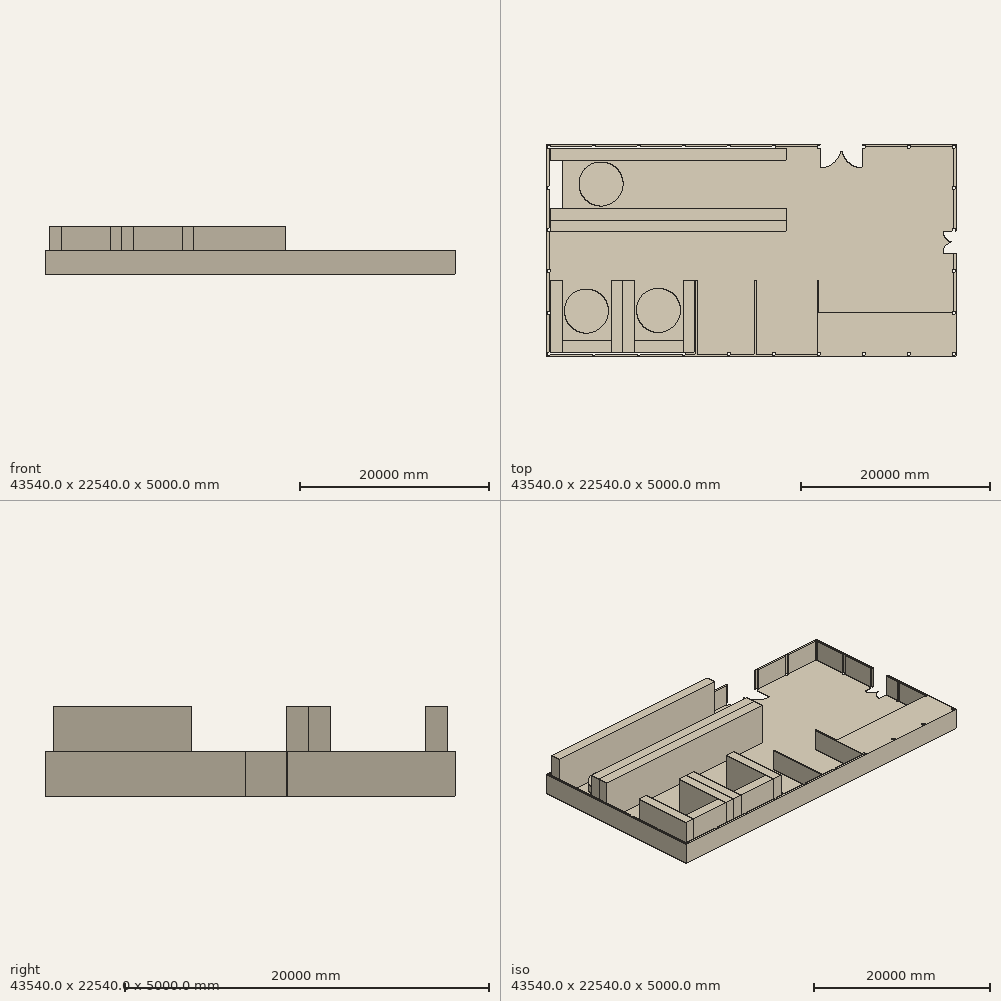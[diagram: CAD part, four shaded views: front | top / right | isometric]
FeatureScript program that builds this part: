
annotation { "Feature Type Name" : "Feature", "Feature Type Description" : "" }
export const myFeature = defineFeature(function(context is Context, id is Id, definition is map)
    precondition{}
    {
        {
            var Q0;
            Q0=qCreatedBy(makeId("Top.planeOp"),FACE);
            var sketch = newSketch(context, id + "F0", { "sketchPlane" : qUnion([Q0])});
            skLineSegment(sketch, "E0", {"start": v(0, 22000) * mm, "end": v(43000, 22000) * mm});
            skLineSegment(sketch, "E1", {"start": v(43000, 22000) * mm, "end": v(43000, 4400) * mm});
            skLineSegment(sketch, "E2", {"start": v(0, 22000) * mm, "end": v(0, 0) * mm});
            skLineSegment(sketch, "E3", {"start": v(0, 0) * mm, "end": v(28666.67, 0) * mm});
            skLineSegment(sketch, "E4.bottom", {"start": v(170, 22170) * mm, "end": v(-170, 22170) * mm});
            skLineSegment(sketch, "E4.top", {"start": v(170, 21830) * mm, "end": v(-170, 21830) * mm});
            skLineSegment(sketch, "E4.left", {"start": v(170, 22170) * mm, "end": v(170, 21830) * mm});
            skLineSegment(sketch, "E4.right", {"start": v(-170, 22170) * mm, "end": v(-170, 21830) * mm});
            skPoint(sketch, "E4.middle", {"position": v(0, 22000) * mm});
            skLineSegment(sketch, "E5.bottom", {"start": v(170, 170) * mm, "end": v(-170, 170) * mm});
            skLineSegment(sketch, "E5.top", {"start": v(170, -170) * mm, "end": v(-170, -170) * mm});
            skLineSegment(sketch, "E5.left", {"start": v(170, 170) * mm, "end": v(170, -170) * mm});
            skLineSegment(sketch, "E5.right", {"start": v(-170, 170) * mm, "end": v(-170, -170) * mm});
            skPoint(sketch, "E5.middle", {"position": v(0, 0) * mm});
            skLineSegment(sketch, "E6.0.1.0", {"start": v(170, 4230) * mm, "end": v(-170, 4230) * mm});
            skLineSegment(sketch, "E6.0.1.1", {"start": v(170, 4570) * mm, "end": v(-170, 4570) * mm});
            skLineSegment(sketch, "E6.0.1.2", {"start": v(170, 4570) * mm, "end": v(170, 4230) * mm});
            skLineSegment(sketch, "E6.0.1.3", {"start": v(-170, 4570) * mm, "end": v(-170, 4230) * mm});
            skLineSegment(sketch, "E6.0.2.0", {"start": v(170, 8630) * mm, "end": v(-170, 8630) * mm});
            skLineSegment(sketch, "E6.0.2.1", {"start": v(170, 8970) * mm, "end": v(-170, 8970) * mm});
            skLineSegment(sketch, "E6.0.2.2", {"start": v(170, 8970) * mm, "end": v(170, 8630) * mm});
            skLineSegment(sketch, "E6.0.2.3", {"start": v(-170, 8970) * mm, "end": v(-170, 8630) * mm});
            skLineSegment(sketch, "E6.0.3.0", {"start": v(170, 13030) * mm, "end": v(-170, 13030) * mm});
            skLineSegment(sketch, "E6.0.3.1", {"start": v(170, 13370) * mm, "end": v(-170, 13370) * mm});
            skLineSegment(sketch, "E6.0.3.2", {"start": v(170, 13370) * mm, "end": v(170, 13030) * mm});
            skLineSegment(sketch, "E6.0.3.3", {"start": v(-170, 13370) * mm, "end": v(-170, 13030) * mm});
            skLineSegment(sketch, "E6.0.4.0", {"start": v(170, 17430) * mm, "end": v(-170, 17430) * mm});
            skLineSegment(sketch, "E6.0.4.1", {"start": v(170, 17770) * mm, "end": v(-170, 17770) * mm});
            skLineSegment(sketch, "E6.0.4.2", {"start": v(170, 17770) * mm, "end": v(170, 17430) * mm});
            skLineSegment(sketch, "E6.0.4.3", {"start": v(-170, 17770) * mm, "end": v(-170, 17430) * mm});
            skLineSegment(sketch, "E7.0.1.0", {"start": v(43170, 4570) * mm, "end": v(43170, 4230) * mm});
            skPoint(sketch, "E7.0.1.1", {"position": v(43000, 4400) * mm});
            skLineSegment(sketch, "E7.0.1.2", {"start": v(42830, 4570) * mm, "end": v(42830, 4230) * mm});
            skLineSegment(sketch, "E7.0.1.4", {"start": v(43170, 4230) * mm, "end": v(42830, 4230) * mm});
            skLineSegment(sketch, "E7.0.1.5", {"start": v(43170, 4570) * mm, "end": v(42830, 4570) * mm});
            skLineSegment(sketch, "E7.0.2.0", {"start": v(43170, 8970) * mm, "end": v(43170, 8630) * mm});
            skPoint(sketch, "E7.0.2.1", {"position": v(43000, 8800) * mm});
            skLineSegment(sketch, "E7.0.2.2", {"start": v(42830, 8970) * mm, "end": v(42830, 8630) * mm});
            skLineSegment(sketch, "E7.0.2.4", {"start": v(43170, 8630) * mm, "end": v(42830, 8630) * mm});
            skLineSegment(sketch, "E7.0.2.5", {"start": v(43170, 8970) * mm, "end": v(42830, 8970) * mm});
            skLineSegment(sketch, "E7.0.3.0", {"start": v(43170, 13370) * mm, "end": v(43170, 13030) * mm});
            skPoint(sketch, "E7.0.3.1", {"position": v(43000, 13200) * mm});
            skLineSegment(sketch, "E7.0.3.2", {"start": v(42830, 13370) * mm, "end": v(42830, 13030) * mm});
            skLineSegment(sketch, "E7.0.3.4", {"start": v(43170, 13030) * mm, "end": v(42830, 13030) * mm});
            skLineSegment(sketch, "E7.0.3.5", {"start": v(43170, 13370) * mm, "end": v(42830, 13370) * mm});
            skLineSegment(sketch, "E7.0.4.0", {"start": v(43170, 17770) * mm, "end": v(43170, 17430) * mm});
            skPoint(sketch, "E7.0.4.1", {"position": v(43000, 17600) * mm});
            skLineSegment(sketch, "E7.0.4.2", {"start": v(42830, 17770) * mm, "end": v(42830, 17430) * mm});
            skLineSegment(sketch, "E7.0.4.4", {"start": v(43170, 17430) * mm, "end": v(42830, 17430) * mm});
            skLineSegment(sketch, "E7.0.4.5", {"start": v(43170, 17770) * mm, "end": v(42830, 17770) * mm});
            skPoint(sketch, "E8.1.0.0", {"position": v(4777.78, 22000) * mm});
            skLineSegment(sketch, "E8.1.0.1", {"start": v(4947.78, 22170) * mm, "end": v(4607.78, 22170) * mm});
            skLineSegment(sketch, "E8.1.0.2", {"start": v(4947.78, 22170) * mm, "end": v(4947.78, 21830) * mm});
            skLineSegment(sketch, "E8.1.0.3", {"start": v(4607.78, 22170) * mm, "end": v(4607.78, 21830) * mm});
            skLineSegment(sketch, "E8.1.0.4", {"start": v(4947.78, 21830) * mm, "end": v(4607.78, 21830) * mm});
            skPoint(sketch, "E8.2.0.0", {"position": v(9555.56, 22000) * mm});
            skLineSegment(sketch, "E8.2.0.1", {"start": v(9725.56, 22170) * mm, "end": v(9385.56, 22170) * mm});
            skLineSegment(sketch, "E8.2.0.2", {"start": v(9725.56, 22170) * mm, "end": v(9725.56, 21830) * mm});
            skLineSegment(sketch, "E8.2.0.3", {"start": v(9385.56, 22170) * mm, "end": v(9385.56, 21830) * mm});
            skLineSegment(sketch, "E8.2.0.4", {"start": v(9725.56, 21830) * mm, "end": v(9385.56, 21830) * mm});
            skPoint(sketch, "E8.3.0.0", {"position": v(14333.33, 22000) * mm});
            skLineSegment(sketch, "E8.3.0.1", {"start": v(14503.33, 22170) * mm, "end": v(14163.33, 22170) * mm});
            skLineSegment(sketch, "E8.3.0.2", {"start": v(14503.33, 22170) * mm, "end": v(14503.33, 21830) * mm});
            skLineSegment(sketch, "E8.3.0.3", {"start": v(14163.33, 22170) * mm, "end": v(14163.33, 21830) * mm});
            skLineSegment(sketch, "E8.3.0.4", {"start": v(14503.33, 21830) * mm, "end": v(14163.33, 21830) * mm});
            skPoint(sketch, "E8.4.0.0", {"position": v(19111.11, 22000) * mm});
            skLineSegment(sketch, "E8.4.0.1", {"start": v(19281.11, 22170) * mm, "end": v(18941.11, 22170) * mm});
            skLineSegment(sketch, "E8.4.0.2", {"start": v(19281.11, 22170) * mm, "end": v(19281.11, 21830) * mm});
            skLineSegment(sketch, "E8.4.0.3", {"start": v(18941.11, 22170) * mm, "end": v(18941.11, 21830) * mm});
            skLineSegment(sketch, "E8.4.0.4", {"start": v(19281.11, 21830) * mm, "end": v(18941.11, 21830) * mm});
            skPoint(sketch, "E8.5.0.0", {"position": v(23888.89, 22000) * mm});
            skLineSegment(sketch, "E8.5.0.1", {"start": v(24058.89, 22170) * mm, "end": v(23718.89, 22170) * mm});
            skLineSegment(sketch, "E8.5.0.2", {"start": v(24058.89, 22170) * mm, "end": v(24058.89, 21830) * mm});
            skLineSegment(sketch, "E8.5.0.3", {"start": v(23718.89, 22170) * mm, "end": v(23718.89, 21830) * mm});
            skLineSegment(sketch, "E8.5.0.4", {"start": v(24058.89, 21830) * mm, "end": v(23718.89, 21830) * mm});
            skPoint(sketch, "E8.6.0.0", {"position": v(28666.67, 22000) * mm});
            skLineSegment(sketch, "E8.6.0.1", {"start": v(28836.67, 22170) * mm, "end": v(28496.67, 22170) * mm});
            skLineSegment(sketch, "E8.6.0.2", {"start": v(28836.67, 22170) * mm, "end": v(28836.67, 21830) * mm});
            skLineSegment(sketch, "E8.6.0.3", {"start": v(28496.67, 22170) * mm, "end": v(28496.67, 21830) * mm});
            skLineSegment(sketch, "E8.6.0.4", {"start": v(28836.67, 21830) * mm, "end": v(28496.67, 21830) * mm});
            skPoint(sketch, "E8.7.0.0", {"position": v(33444.44, 22000) * mm});
            skLineSegment(sketch, "E8.7.0.1", {"start": v(33614.44, 22170) * mm, "end": v(33274.44, 22170) * mm});
            skLineSegment(sketch, "E8.7.0.2", {"start": v(33614.44, 22170) * mm, "end": v(33614.44, 21830) * mm});
            skLineSegment(sketch, "E8.7.0.3", {"start": v(33274.44, 22170) * mm, "end": v(33274.44, 21830) * mm});
            skLineSegment(sketch, "E8.7.0.4", {"start": v(33614.44, 21830) * mm, "end": v(33274.44, 21830) * mm});
            skPoint(sketch, "E8.8.0.0", {"position": v(38222.22, 22000) * mm});
            skLineSegment(sketch, "E8.8.0.1", {"start": v(38392.22, 22170) * mm, "end": v(38052.22, 22170) * mm});
            skLineSegment(sketch, "E8.8.0.2", {"start": v(38392.22, 22170) * mm, "end": v(38392.22, 21830) * mm});
            skLineSegment(sketch, "E8.8.0.3", {"start": v(38052.22, 22170) * mm, "end": v(38052.22, 21830) * mm});
            skLineSegment(sketch, "E8.8.0.4", {"start": v(38392.22, 21830) * mm, "end": v(38052.22, 21830) * mm});
            skPoint(sketch, "E8.9.0.0", {"position": v(43000, 22000) * mm});
            skLineSegment(sketch, "E8.9.0.1", {"start": v(43170, 22170) * mm, "end": v(42830, 22170) * mm});
            skLineSegment(sketch, "E8.9.0.2", {"start": v(43170, 22170) * mm, "end": v(43170, 21830) * mm});
            skLineSegment(sketch, "E8.9.0.3", {"start": v(42830, 22170) * mm, "end": v(42830, 21830) * mm});
            skLineSegment(sketch, "E8.9.0.4", {"start": v(43170, 21830) * mm, "end": v(42830, 21830) * mm});
            skLineSegment(sketch, "E9.1.0.0", {"start": v(4947.78, 170) * mm, "end": v(4607.78, 170) * mm});
            skLineSegment(sketch, "E9.1.0.1", {"start": v(4947.78, -170) * mm, "end": v(4607.78, -170) * mm});
            skPoint(sketch, "E9.1.0.2", {"position": v(4777.78, 0) * mm});
            skLineSegment(sketch, "E9.1.0.3", {"start": v(4607.78, 170) * mm, "end": v(4607.78, -170) * mm});
            skLineSegment(sketch, "E9.1.0.4", {"start": v(4947.78, 170) * mm, "end": v(4947.78, -170) * mm});
            skLineSegment(sketch, "E9.2.0.0", {"start": v(9725.56, 170) * mm, "end": v(9385.56, 170) * mm});
            skLineSegment(sketch, "E9.2.0.1", {"start": v(9725.56, -170) * mm, "end": v(9385.56, -170) * mm});
            skPoint(sketch, "E9.2.0.2", {"position": v(9555.56, 0) * mm});
            skLineSegment(sketch, "E9.2.0.3", {"start": v(9385.56, 170) * mm, "end": v(9385.56, -170) * mm});
            skLineSegment(sketch, "E9.2.0.4", {"start": v(9725.56, 170) * mm, "end": v(9725.56, -170) * mm});
            skLineSegment(sketch, "E9.3.0.0", {"start": v(14503.33, 170) * mm, "end": v(14163.33, 170) * mm});
            skLineSegment(sketch, "E9.3.0.1", {"start": v(14503.33, -170) * mm, "end": v(14163.33, -170) * mm});
            skPoint(sketch, "E9.3.0.2", {"position": v(14333.33, 0) * mm});
            skLineSegment(sketch, "E9.3.0.3", {"start": v(14163.33, 170) * mm, "end": v(14163.33, -170) * mm});
            skLineSegment(sketch, "E9.3.0.4", {"start": v(14503.33, 170) * mm, "end": v(14503.33, -170) * mm});
            skLineSegment(sketch, "E9.4.0.0", {"start": v(19281.11, 170) * mm, "end": v(18941.11, 170) * mm});
            skLineSegment(sketch, "E9.4.0.1", {"start": v(19281.11, -170) * mm, "end": v(18941.11, -170) * mm});
            skPoint(sketch, "E9.4.0.2", {"position": v(19111.11, 0) * mm});
            skLineSegment(sketch, "E9.4.0.3", {"start": v(18941.11, 170) * mm, "end": v(18941.11, -170) * mm});
            skLineSegment(sketch, "E9.4.0.4", {"start": v(19281.11, 170) * mm, "end": v(19281.11, -170) * mm});
            skLineSegment(sketch, "E9.5.0.0", {"start": v(24058.89, 170) * mm, "end": v(23718.89, 170) * mm});
            skLineSegment(sketch, "E9.5.0.1", {"start": v(24058.89, -170) * mm, "end": v(23718.89, -170) * mm});
            skPoint(sketch, "E9.5.0.2", {"position": v(23888.89, 0) * mm});
            skLineSegment(sketch, "E9.5.0.3", {"start": v(23718.89, 170) * mm, "end": v(23718.89, -170) * mm});
            skLineSegment(sketch, "E9.5.0.4", {"start": v(24058.89, 170) * mm, "end": v(24058.89, -170) * mm});
            skLineSegment(sketch, "E9.6.0.0", {"start": v(28836.67, 170) * mm, "end": v(28496.67, 170) * mm});
            skLineSegment(sketch, "E9.6.0.1", {"start": v(28836.67, -170) * mm, "end": v(28496.67, -170) * mm});
            skPoint(sketch, "E9.6.0.2", {"position": v(28666.67, 0) * mm});
            skLineSegment(sketch, "E9.6.0.3", {"start": v(28496.67, 170) * mm, "end": v(28496.67, -170) * mm});
            skLineSegment(sketch, "E9.6.0.4", {"start": v(28836.67, 170) * mm, "end": v(28836.67, -170) * mm});
            skLineSegment(sketch, "E9.7.0.0", {"start": v(33614.44, 170) * mm, "end": v(33274.44, 170) * mm});
            skLineSegment(sketch, "E9.7.0.1", {"start": v(33614.44, -170) * mm, "end": v(33274.44, -170) * mm});
            skPoint(sketch, "E9.7.0.2", {"position": v(33444.44, 0) * mm});
            skLineSegment(sketch, "E9.7.0.3", {"start": v(33274.44, 170) * mm, "end": v(33274.44, -170) * mm});
            skLineSegment(sketch, "E9.7.0.4", {"start": v(33614.44, 170) * mm, "end": v(33614.44, -170) * mm});
            skLineSegment(sketch, "E9.8.0.0", {"start": v(38392.22, 170) * mm, "end": v(38052.22, 170) * mm});
            skLineSegment(sketch, "E9.8.0.1", {"start": v(38392.22, -170) * mm, "end": v(38052.22, -170) * mm});
            skPoint(sketch, "E9.8.0.2", {"position": v(38222.22, 0) * mm});
            skLineSegment(sketch, "E9.8.0.3", {"start": v(38052.22, 170) * mm, "end": v(38052.22, -170) * mm});
            skLineSegment(sketch, "E9.8.0.4", {"start": v(38392.22, 170) * mm, "end": v(38392.22, -170) * mm});
            skLineSegment(sketch, "E9.9.0.0", {"start": v(43170, 170) * mm, "end": v(42830, 170) * mm});
            skLineSegment(sketch, "E9.9.0.1", {"start": v(43170, -170) * mm, "end": v(42830, -170) * mm});
            skPoint(sketch, "E9.9.0.2", {"position": v(43000, 0) * mm});
            skLineSegment(sketch, "E9.9.0.3", {"start": v(42830, 170) * mm, "end": v(42830, -170) * mm});
            skLineSegment(sketch, "E9.9.0.4", {"start": v(43170, 170) * mm, "end": v(43170, -170) * mm});
            skLineSegment(sketch, "E10.bottom", {"start": v(28836.67, 22000) * mm, "end": v(33274.44, 22000) * mm});
            skLineSegment(sketch, "E10.left", {"start": v(28836.67, 22000) * mm, "end": v(28836.67, 19781.11) * mm});
            skLineSegment(sketch, "E10.right", {"start": v(33274.44, 22000) * mm, "end": v(33274.44, 19781.11) * mm});
            skLineSegment(sketch, "E11", {"start": v(28666.67, 0) * mm, "end": v(43000, 0) * mm});
            skLineSegment(sketch, "E12", {"start": v(43000, 4400) * mm, "end": v(43000, 0) * mm});
            skLineSegment(sketch, "E13", {"start": v(43000, 4400) * mm, "end": v(28666.67, 4400) * mm});
            skLineSegment(sketch, "E14", {"start": v(28666.67, 4400) * mm, "end": v(28666.67, 0) * mm});
            skLineSegment(sketch, "E15", {"start": v(33444.44, 0) * mm, "end": v(33444.44, 4400) * mm});
            skLineSegment(sketch, "E16.top", {"start": v(43000, 10730) * mm, "end": v(41850, 10730) * mm});
            skLineSegment(sketch, "E16.left", {"start": v(43000, 13030) * mm, "end": v(43000, 10730) * mm});
            skLineSegment(sketch, "E17.top", {"start": v(69479.6, 14575.56) * mm, "end": v(70779.6, 14575.56) * mm});
            skLineSegment(sketch, "E17.left", {"start": v(69479.6, 17475.56) * mm, "end": v(69479.6, 14575.56) * mm});
            skLineSegment(sketch, "E17.right", {"start": v(70779.6, 17475.56) * mm, "end": v(70779.6, 14575.56) * mm});
            skLineSegment(sketch, "E18", {"start": v(69479.6, 17475.56) * mm, "end": v(69704.6, 17475.56) * mm});
            skLineSegment(sketch, "E19.MirrorCS", {"start": v(69904.6, 17475.56) * mm, "end": v(69904.6, 19075.56) * mm});
            skLineSegment(sketch, "E20", {"start": v(69704.6, 19075.56) * mm, "end": v(69704.6, 17475.56) * mm});
            skLineSegment(sketch, "E21.MirrorCS", {"start": v(70354.6, 17475.56) * mm, "end": v(70354.6, 19075.56) * mm});
            skLineSegment(sketch, "E22.MirrorCS", {"start": v(70554.6, 19075.56) * mm, "end": v(70554.6, 17475.56) * mm});
            skLineSegment(sketch, "E23", {"start": v(69704.6, 19075.56) * mm, "end": v(69904.6, 19075.56) * mm});
            skLineSegment(sketch, "E24.trimOffspring", {"start": v(70354.6, 19075.56) * mm, "end": v(70554.6, 19075.56) * mm});
            skLineSegment(sketch, "E25.bottom", {"start": v(64498.07, 14575.56) * mm, "end": v(65798.07, 14575.56) * mm});
            skLineSegment(sketch, "E25.top", {"start": v(64498.07, 19075.56) * mm, "end": v(65798.07, 19075.56) * mm});
            skLineSegment(sketch, "E25.left", {"start": v(64498.07, 14575.56) * mm, "end": v(64498.07, 19075.56) * mm});
            skLineSegment(sketch, "E25.right", {"start": v(65798.07, 14575.56) * mm, "end": v(65798.07, 19075.56) * mm});
            skLineSegment(sketch, "E26.trimOffspring", {"start": v(69904.6, 17475.56) * mm, "end": v(70354.6, 17475.56) * mm});
            skLineSegment(sketch, "E27.trimOffspring", {"start": v(70554.6, 17475.56) * mm, "end": v(70779.6, 17475.56) * mm});
            skLineSegment(sketch, "E28", {"start": v(30055.67, 19781.11) * mm, "end": v(30055.67, 11370) * mm});
            skLineSegment(sketch, "E29", {"start": v(30055.67, 11370) * mm, "end": v(0, 11370) * mm});
            skLineSegment(sketch, "E30", {"start": v(0, 9370) * mm, "end": v(32055.67, 9370) * mm});
            skLineSegment(sketch, "E31", {"start": v(32055.67, 9370) * mm, "end": v(32055.67, 19781.11) * mm});
            skLineSegment(sketch, "E32", {"start": v(31055.56, 19781.11) * mm, "end": v(31055.56, 10370) * mm, "construction": true});
            skLineSegment(sketch, "E33", {"start": v(31055.56, 10370) * mm, "end": v(0, 10370) * mm, "construction": true});
            skArc(sketch, "E34", {"start": v(43000, 11880) * mm, "mid": v(42186.83, 12216.83) * mm, "end": v(41850, 13030) * mm});
            skLineSegment(sketch, "E35", {"start": v(41850, 13030) * mm, "end": v(43000, 13030) * mm});
            skArc(sketch, "E36", {"start": v(43000, 11880) * mm, "mid": v(42186.83, 11543.17) * mm, "end": v(41850, 10730) * mm});
            skArc(sketch, "E37", {"start": v(31055.56, 22000) * mm, "mid": v(30405.66, 20431) * mm, "end": v(28836.67, 19781.11) * mm});
            skArc(sketch, "E38", {"start": v(31055.56, 22000) * mm, "mid": v(31705.45, 20431) * mm, "end": v(33274.44, 19781.11) * mm});
            skLineSegment(sketch, "E39", {"start": v(28836.67, 19781.11) * mm, "end": v(33274.44, 19781.11) * mm, "construction": true});
            skPoint(sketch, "E40", {"position": v(32055.67, 14575.56) * mm});
            skLineSegment(sketch, "E41", {"start": v(28666.67, 4400) * mm, "end": v(28666.67, 7770) * mm});
            skLineSegment(sketch, "E42.3", {"start": v(15589.43, -270) * mm, "end": v(15589.43, 7770) * mm});
            skLineSegment(sketch, "E43.0", {"start": v(22016.67, 7770) * mm, "end": v(22016.67, -270) * mm});
            skLineSegment(sketch, "E44.bottom", {"start": v(-270, 22270) * mm, "end": v(43270, 22270) * mm});
            skLineSegment(sketch, "E44.top", {"start": v(-270, -270) * mm, "end": v(43270, -270) * mm});
            skLineSegment(sketch, "E44.left", {"start": v(-270, 22270) * mm, "end": v(-270, -270) * mm});
            skLineSegment(sketch, "E44.right", {"start": v(43270, 22270) * mm, "end": v(43270, -270) * mm});
            skLineSegment(sketch, "E45", {"start": v(33274.44, 22170) * mm, "end": v(33274.44, 22270) * mm});
            skLineSegment(sketch, "E46", {"start": v(28836.67, 22170) * mm, "end": v(28836.67, 22270) * mm});
            skLineSegment(sketch, "E47", {"start": v(43170, 13030) * mm, "end": v(43270, 13030) * mm});
            skLineSegment(sketch, "E48", {"start": v(43000, 10730) * mm, "end": v(43270, 10730) * mm});
            skLineSegment(sketch, "E49.bottom", {"start": v(170, 21830) * mm, "end": v(25170, 21830) * mm});
            skLineSegment(sketch, "E49.top", {"start": v(170, 20610) * mm, "end": v(25170, 20610) * mm});
            skLineSegment(sketch, "E49.left", {"start": v(170, 21830) * mm, "end": v(170, 20610) * mm});
            skLineSegment(sketch, "E49.right", {"start": v(25170, 21830) * mm, "end": v(25170, 20610) * mm});
            skLineSegment(sketch, "E50.bottom", {"start": v(170, 15410) * mm, "end": v(25170, 15410) * mm});
            skLineSegment(sketch, "E50.top", {"start": v(170, 14190) * mm, "end": v(25170, 14190) * mm});
            skLineSegment(sketch, "E50.left", {"start": v(170, 15410) * mm, "end": v(170, 14190) * mm});
            skLineSegment(sketch, "E50.right", {"start": v(25170, 15410) * mm, "end": v(25170, 14190) * mm});
            skLineSegment(sketch, "E51", {"start": v(170, 14190) * mm, "end": v(170, 12970) * mm});
            skLineSegment(sketch, "E52", {"start": v(170, 12970) * mm, "end": v(25170, 12970) * mm});
            skLineSegment(sketch, "E53", {"start": v(25170, 12970) * mm, "end": v(25170, 14190) * mm});
            skLineSegment(sketch, "E54.bottom", {"start": v(170, 170) * mm, "end": v(1390, 170) * mm});
            skLineSegment(sketch, "E54.top", {"start": v(170, 7770) * mm, "end": v(1390, 7770) * mm});
            skLineSegment(sketch, "E54.left", {"start": v(170, 170) * mm, "end": v(170, 7770) * mm});
            skLineSegment(sketch, "E54.right", {"start": v(1390, 170) * mm, "end": v(1390, 7770) * mm});
            skLineSegment(sketch, "E55.bottom", {"start": v(1390, 170) * mm, "end": v(6590, 170) * mm});
            skLineSegment(sketch, "E55.top", {"start": v(1390, 1390) * mm, "end": v(6590, 1390) * mm});
            skLineSegment(sketch, "E55.left", {"start": v(1390, 170) * mm, "end": v(1390, 1390) * mm});
            skLineSegment(sketch, "E55.right", {"start": v(6590, 170) * mm, "end": v(6590, 1390) * mm});
            skLineSegment(sketch, "E56.bottom", {"start": v(6590, 170) * mm, "end": v(7810, 170) * mm});
            skLineSegment(sketch, "E56.top", {"start": v(6590, 7770) * mm, "end": v(7810, 7770) * mm});
            skLineSegment(sketch, "E56.left", {"start": v(6590, 170) * mm, "end": v(6590, 7770) * mm});
            skLineSegment(sketch, "E56.right", {"start": v(7810, 170) * mm, "end": v(7810, 7770) * mm});
            skLineSegment(sketch, "E57.bottom", {"start": v(7810, 170) * mm, "end": v(9030, 170) * mm});
            skLineSegment(sketch, "E57.top", {"start": v(7810, 7770) * mm, "end": v(9030, 7770) * mm});
            skLineSegment(sketch, "E57.right", {"start": v(9030, 170) * mm, "end": v(9030, 7770) * mm});
            skLineSegment(sketch, "E58.bottom", {"start": v(9030, 170) * mm, "end": v(14230, 170) * mm});
            skLineSegment(sketch, "E58.top", {"start": v(9030, 1390) * mm, "end": v(14230, 1390) * mm});
            skLineSegment(sketch, "E58.left", {"start": v(9030, 170) * mm, "end": v(9030, 1390) * mm});
            skLineSegment(sketch, "E58.right", {"start": v(14230, 170) * mm, "end": v(14230, 1390) * mm});
            skLineSegment(sketch, "E59.bottom", {"start": v(14230, 170) * mm, "end": v(15450, 170) * mm});
            skLineSegment(sketch, "E59.top", {"start": v(14230, 7770) * mm, "end": v(15450, 7770) * mm});
            skLineSegment(sketch, "E59.left", {"start": v(14230, 170) * mm, "end": v(14230, 7770) * mm});
            skLineSegment(sketch, "E59.right", {"start": v(15450, 170) * mm, "end": v(15450, 7770) * mm});
            skLineSegment(sketch, "E60.bottom", {"start": v(170, 20610) * mm, "end": v(1390, 20610) * mm});
            skLineSegment(sketch, "E60.top", {"start": v(170, 15410) * mm, "end": v(1390, 15410) * mm});
            skLineSegment(sketch, "E60.left", {"start": v(170, 20610) * mm, "end": v(170, 15410) * mm});
            skLineSegment(sketch, "E60.right", {"start": v(1390, 20610) * mm, "end": v(1390, 15410) * mm});
            skLineSegment(sketch, "E61", {"start": v(64498.07, 19075.56) * mm, "end": v(65798.07, 14575.56) * mm, "construction": true});
            skCircle(sketch, "E62", {"center": v(5527.86, 18056.06) * mm, "radius": 2342 * mm});
            skPoint(sketch, "E42.0.start.orphan", {"position": v(28516.67, -13106.31) * mm});
            skLineSegment(sketch, "E63", {"start": v(15589.43, 7770) * mm, "end": v(22016.67, 7770) * mm});
            skLineSegment(sketch, "E64", {"start": v(22016.67, 7770) * mm, "end": v(28666.67, 7770) * mm});
            skLineSegment(sketch, "E65", {"start": v(15739.43, -270) * mm, "end": v(15739.43, 7770) * mm});
            skLineSegment(sketch, "E66", {"start": v(15589.43, 7620) * mm, "end": v(28666.67, 7620) * mm});
            skLineSegment(sketch, "E67", {"start": v(28516.67, 7770) * mm, "end": v(28516.67, -270) * mm});
            skLineSegment(sketch, "E68", {"start": v(21866.67, 7770) * mm, "end": v(21866.67, -270) * mm});
            skCircle(sketch, "E69", {"center": v(11629.68, 4634.86) * mm, "radius": 2342 * mm});
            skCircle(sketch, "E70", {"center": v(3977.19, 4560.05) * mm, "radius": 2342 * mm});
            skSolve(sketch);
        }
        {
            var Q0;
            {var subQ69=sQuery(id+"F0.wireOp",EDGE,"E6.0.2.2");Q0=makeQuery(id+"F0.imprint","IMPRINT",FACE,{"disambiguationData":[TD([[makeQuery(id+"F0.imprint","IMPRINT",EDGE,{"derivedFrom":subQ69}),1.0]])]});}
            var Q1;
            {var subQ0=sQuery(id+"F0.wireOp",EDGE,"E9.4.0.0");Q1=makeQuery(id+"F0.imprint","IMPRINT",FACE,{"disambiguationData":[TD([[makeQuery(id+"F0.imprint","IMPRINT",EDGE,{"derivedFrom":subQ0}),-1.0]])]});}
            var Q2;
            {var subQ1=sQuery(id+"F0.wireOp",EDGE,"E9.5.0.0");Q2=makeQuery(id+"F0.imprint","IMPRINT",FACE,{"disambiguationData":[TD([[makeQuery(id+"F0.imprint","IMPRINT",EDGE,{"derivedFrom":subQ1}),-1.0]])]});}
            var Q3;
            {var subQ1=sQuery(id+"F0.wireOp",EDGE,"E43.0");var subQ3=sQuery(id+"F0.wireOp",EDGE,"E66");var subQ4=makeQuery(id+"F0.imprint","INTERSECT",VERTEX,{"derivedFrom":[subQ1,subQ3]});Q3=makeQuery(id+"F0.imprint","IMPRINT",FACE,{"disambiguationData":[TD([[makeQuery(id+"F0.imprint","IMPRINT",EDGE,{"disambiguationData":[TD([[subQ4,-1.0]])],"derivedFrom":subQ3}),1.0]])]});}
            var Q4;
            {var subQ0=sQuery(id+"F0.wireOp",EDGE,"E65");var subQ1=sQuery(id+"F0.wireOp",EDGE,"E63");var subQ2=makeQuery(id+"F0.imprint","INTERSECT",VERTEX,{"derivedFrom":[subQ1,subQ0]});Q4=makeQuery(id+"F0.imprint","IMPRINT",FACE,{"disambiguationData":[TD([[makeQuery(id+"F0.imprint","IMPRINT",EDGE,{"disambiguationData":[TD([[subQ2,-1.0]])],"derivedFrom":subQ1}),-1.0]])]});}
            extrude(context, id + "F1", {"entities" : qUnion([Q0, Q1, Q2, Q3, Q4]), "depth" : 25 * mm, "offsetDistance" : 25 * mm});
        }
        {
            var Q0;
            Q0=makeQuery(id+"F0.imprint","IMPRINT",FACE,{"disambiguationData":[TD([[makeQuery(id+"F0.imprint","IMPRINT",EDGE,{"derivedFrom":sQuery(id+"F0.wireOp",EDGE,"E50.bottom")}),-1.0]])]});
            var Q1;
            {var subQ3=sQuery(id+"F0.wireOp",EDGE,"E54.bottom");Q1=makeQuery(id+"F0.imprint","IMPRINT",FACE,{"disambiguationData":[TD([[makeQuery(id+"F0.imprint","IMPRINT",EDGE,{"derivedFrom":subQ3}),1.0]])]});}
            var Q2;
            {var subQ3=sQuery(id+"F0.wireOp",EDGE,"E56.bottom");Q2=makeQuery(id+"F0.imprint","IMPRINT",FACE,{"disambiguationData":[TD([[makeQuery(id+"F0.imprint","IMPRINT",EDGE,{"derivedFrom":subQ3}),1.0]])]});}
            var Q3;
            Q3=makeQuery(id+"F0.imprint","IMPRINT",FACE,{"disambiguationData":[TD([[makeQuery(id+"F0.imprint","IMPRINT",EDGE,{"derivedFrom":sQuery(id+"F0.wireOp",EDGE,"E49.top")}),1.0]])]});
            var Q4;
            {var subQ4=sQuery(id+"F0.wireOp",EDGE,"E59.top");Q4=makeQuery(id+"F0.imprint","IMPRINT",FACE,{"disambiguationData":[TD([[makeQuery(id+"F0.imprint","IMPRINT",EDGE,{"derivedFrom":subQ4}),-1.0]])]});}
            extrude(context, id + "F2", {"entities" : qUnion([Q0, Q1, Q2, Q3, Q4]), "depth" : 5000 * mm, "offsetDistance" : 25 * mm});
        }
        {
            var Q0;
            {var subQ0=sQuery(id+"F0.wireOp",EDGE,"E55.top");Q0=makeQuery(id+"F0.imprint","IMPRINT",FACE,{"disambiguationData":[TD([[makeQuery(id+"F0.imprint","IMPRINT",EDGE,{"derivedFrom":subQ0}),-1.0]])]});}
            var Q1;
            Q1=makeQuery(id+"F0.imprint","IMPRINT",FACE,{"disambiguationData":[TD([[makeQuery(id+"F0.imprint","IMPRINT",EDGE,{"derivedFrom":sQuery(id+"F0.wireOp",EDGE,"E57.bottom")}),1.0]])]});
            var Q2;
            {var subQ3=sQuery(id+"F0.wireOp",EDGE,"E50.top");Q2=makeQuery(id+"F0.imprint","IMPRINT",FACE,{"disambiguationData":[TD([[makeQuery(id+"F0.imprint","IMPRINT",EDGE,{"derivedFrom":subQ3}),-1.0]])]});}
            var Q3;
            {var subQ3=sQuery(id+"F0.wireOp",EDGE,"E60.bottom");Q3=makeQuery(id+"F0.imprint","IMPRINT",FACE,{"disambiguationData":[TD([[makeQuery(id+"F0.imprint","IMPRINT",EDGE,{"derivedFrom":subQ3}),-1.0]])]});}
            extrude(context, id + "F3", {"entities" : qUnion([Q0, Q1, Q2, Q3]), "depth" : 5000 * mm, "offsetDistance" : 25 * mm});
        }
        {
            var Q0;
            {var subQ7=sQuery(id+"F0.wireOp",EDGE,"E58.top");Q0=makeQuery(id+"F0.imprint","IMPRINT",FACE,{"disambiguationData":[TD([[makeQuery(id+"F0.imprint","IMPRINT",EDGE,{"derivedFrom":subQ7}),-1.0]])]});}
            extrude(context, id + "F4", {"entities" : qUnion([Q0]), "depth" : 5000 * mm, "offsetDistance" : 25 * mm});
        }
        {
            var Q0;
            {var subQ0=sQuery(id+"F0.wireOp",EDGE,"E42.3");var subQ1=sQuery(id+"F0.wireOp",EDGE,"E3");var subQ2=makeQuery(id+"F0.imprint","INTERSECT",VERTEX,{"derivedFrom":[subQ1,subQ0]});Q0=makeQuery(id+"F0.imprint","IMPRINT",FACE,{"disambiguationData":[TD([[makeQuery(id+"F0.imprint","IMPRINT",EDGE,{"disambiguationData":[TD([[subQ2,-1.0]])],"derivedFrom":subQ1}),1.0]])]});}
            var Q1;
            {var subQ0=sQuery(id+"F0.wireOp",EDGE,"E63");var subQ1=sQuery(id+"F0.wireOp",EDGE,"E42.3");var subQ2=makeQuery(id+"F0.imprint","INTERSECT",VERTEX,{"derivedFrom":[subQ1,subQ0]});Q1=makeQuery(id+"F0.imprint","IMPRINT",FACE,{"disambiguationData":[TD([[makeQuery(id+"F0.imprint","IMPRINT",EDGE,{"disambiguationData":[TD([[subQ2,1.0]])],"derivedFrom":subQ1}),-1.0]])]});}
            var Q2;
            {var subQ1=sQuery(id+"F0.wireOp",EDGE,"E43.0");var subQ3=sQuery(id+"F0.wireOp",EDGE,"E66");var subQ4=makeQuery(id+"F0.imprint","INTERSECT",VERTEX,{"derivedFrom":[subQ1,subQ3]});Q2=makeQuery(id+"F0.imprint","IMPRINT",FACE,{"disambiguationData":[TD([[makeQuery(id+"F0.imprint","IMPRINT",EDGE,{"disambiguationData":[TD([[subQ4,1.0]])],"derivedFrom":subQ3}),1.0]])]});}
            var Q3;
            {var subQ0=sQuery(id+"F0.wireOp",EDGE,"E68");var subQ1=sQuery(id+"F0.wireOp",EDGE,"E3");var subQ2=makeQuery(id+"F0.imprint","INTERSECT",VERTEX,{"derivedFrom":[subQ1,subQ0]});Q3=makeQuery(id+"F0.imprint","IMPRINT",FACE,{"disambiguationData":[TD([[makeQuery(id+"F0.imprint","IMPRINT",EDGE,{"disambiguationData":[TD([[subQ2,-1.0]])],"derivedFrom":subQ1}),1.0]])]});}
            var Q4;
            {var subQ0=sQuery(id+"F0.wireOp",EDGE,"E64");var subQ1=sQuery(id+"F0.wireOp",EDGE,"E41");var subQ2=makeQuery(id+"F0.imprint","INTERSECT",VERTEX,{"derivedFrom":[subQ1,subQ0]});Q4=makeQuery(id+"F0.imprint","IMPRINT",FACE,{"disambiguationData":[TD([[makeQuery(id+"F0.imprint","IMPRINT",EDGE,{"disambiguationData":[TD([[subQ2,1.0]])],"derivedFrom":subQ1}),1.0]])]});}
            var Q5;
            {var subQ5=sQuery(id+"F0.wireOp",EDGE,"E14");var subQ7=sQuery(id+"F0.wireOp",EDGE,"E9.6.0.0");var subQ8=makeQuery(id+"F0.imprint","INTERSECT",VERTEX,{"derivedFrom":[subQ7,subQ5]});Q5=makeQuery(id+"F0.imprint","IMPRINT",FACE,{"disambiguationData":[TD([[makeQuery(id+"F0.imprint","IMPRINT",EDGE,{"disambiguationData":[TD([[subQ8,-1.0]])],"derivedFrom":subQ7}),-1.0]])]});}
            extrude(context, id + "F5", {"entities" : qUnion([Q0, Q1, Q2, Q3, Q4, Q5]), "operationType" : NewBodyOperationType.ADD, "depth" : 2500 * mm, "offsetDistance" : 25 * mm});
        }
        {
            var Q0;
            {var subQ5=sQuery(id+"F0.wireOp",EDGE,"E9.6.0.4");var subQ6=sQuery(id+"F0.wireOp",EDGE,"E9.6.0.0");var subQ7=makeQuery(id+"F0.imprint","INTERSECT",VERTEX,{"derivedFrom":[subQ6,subQ5]});Q0=makeQuery(id+"F0.imprint","IMPRINT",FACE,{"disambiguationData":[TD([[makeQuery(id+"F0.imprint","IMPRINT",EDGE,{"disambiguationData":[TD([[subQ7,-1.0]])],"derivedFrom":subQ6}),-1.0]])]});}
            extrude(context, id + "F6", {"entities" : qUnion([Q0]), "depth" : 2500 * mm, "offsetDistance" : 25 * mm});
        }
        {
            var Q0;
            {var subQ11=sQuery(id+"F0.wireOp",EDGE,"E9.8.0.0");Q0=makeQuery(id+"F0.imprint","IMPRINT",FACE,{"disambiguationData":[TD([[makeQuery(id+"F0.imprint","IMPRINT",EDGE,{"derivedFrom":subQ11}),-1.0]])]});}
            extrude(context, id + "F7", {"entities" : qUnion([Q0]), "depth" : 2500 * mm, "offsetDistance" : 25 * mm});
        }
        {
            var Q0;
            Q0=makeQuery(id+"F0.imprint","IMPRINT",FACE,{"disambiguationData":[TD([[makeQuery(id+"F0.imprint","IMPRINT",EDGE,{"derivedFrom":sQuery(id+"F0.wireOp",EDGE,"E62")}),1.0]])]});
            var Q1;
            Q1=makeQuery(id+"F0.imprint","IMPRINT",FACE,{"disambiguationData":[TD([[makeQuery(id+"F0.imprint","IMPRINT",EDGE,{"derivedFrom":sQuery(id+"F0.wireOp",EDGE,"E70")}),1.0]])]});
            var Q2;
            Q2=makeQuery(id+"F0.imprint","IMPRINT",FACE,{"disambiguationData":[TD([[makeQuery(id+"F0.imprint","IMPRINT",EDGE,{"derivedFrom":sQuery(id+"F0.wireOp",EDGE,"E69")}),1.0]])]});
            extrude(context, id + "F8", {"entities" : qUnion([Q0, Q1, Q2]), "depth" : 1000 * mm, "offsetDistance" : 25 * mm});
        }
        {
            var Q0;
            {var subQ14=sQuery(id+"F0.wireOp",EDGE,"E7.0.1.0");Q0=makeQuery(id+"F0.imprint","IMPRINT",FACE,{"disambiguationData":[TD([[makeQuery(id+"F0.imprint","IMPRINT",EDGE,{"derivedFrom":subQ14}),1.0]])]});}
            var Q1;
            {var subQ17=sQuery(id+"F0.wireOp",EDGE,"E7.0.3.0");Q1=makeQuery(id+"F0.imprint","IMPRINT",FACE,{"disambiguationData":[TD([[makeQuery(id+"F0.imprint","IMPRINT",EDGE,{"derivedFrom":subQ17}),1.0]])]});}
            var Q2;
            {var subQ1=sQuery(id+"F0.wireOp",EDGE,"E9.5.0.1");Q2=makeQuery(id+"F0.imprint","IMPRINT",FACE,{"disambiguationData":[TD([[makeQuery(id+"F0.imprint","IMPRINT",EDGE,{"derivedFrom":subQ1}),1.0]])]});}
            var Q3;
            {var subQ1=sQuery(id+"F0.wireOp",EDGE,"E9.4.0.1");Q3=makeQuery(id+"F0.imprint","IMPRINT",FACE,{"disambiguationData":[TD([[makeQuery(id+"F0.imprint","IMPRINT",EDGE,{"derivedFrom":subQ1}),1.0]])]});}
            var Q4;
            {var subQ0=sQuery(id+"F0.wireOp",EDGE,"E68");var subQ1=sQuery(id+"F0.wireOp",EDGE,"E3");var subQ2=makeQuery(id+"F0.imprint","INTERSECT",VERTEX,{"derivedFrom":[subQ1,subQ0]});Q4=makeQuery(id+"F0.imprint","IMPRINT",FACE,{"disambiguationData":[TD([[makeQuery(id+"F0.imprint","IMPRINT",EDGE,{"disambiguationData":[TD([[subQ2,-1.0]])],"derivedFrom":subQ1}),-1.0]])]});}
            var Q5;
            {var subQ0=sQuery(id+"F0.wireOp",EDGE,"E42.3");var subQ1=sQuery(id+"F0.wireOp",EDGE,"E3");var subQ2=makeQuery(id+"F0.imprint","INTERSECT",VERTEX,{"derivedFrom":[subQ1,subQ0]});Q5=makeQuery(id+"F0.imprint","IMPRINT",FACE,{"disambiguationData":[TD([[makeQuery(id+"F0.imprint","IMPRINT",EDGE,{"disambiguationData":[TD([[subQ2,-1.0]])],"derivedFrom":subQ1}),-1.0]])]});}
            var Q6;
            {var subQ73=sQuery(id+"F0.wireOp",EDGE,"E4.bottom");Q6=makeQuery(id+"F0.imprint","IMPRINT",FACE,{"disambiguationData":[TD([[makeQuery(id+"F0.imprint","IMPRINT",EDGE,{"derivedFrom":subQ73}),-1.0]])]});}
            extrude(context, id + "F9", {"entities" : qUnion([Q0, Q1, Q2, Q3, Q4, Q5, Q6]), "operationType" : NewBodyOperationType.ADD, "depth" : 2500 * mm, "offsetDistance" : 25 * mm});
        }
    });
